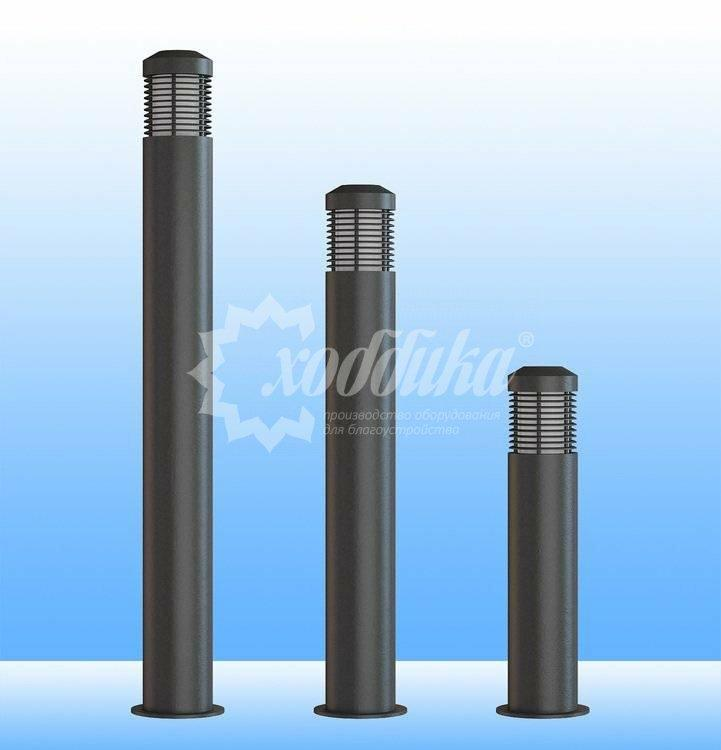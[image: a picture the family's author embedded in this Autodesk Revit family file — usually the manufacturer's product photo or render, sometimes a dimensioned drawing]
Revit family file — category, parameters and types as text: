
# Revit family: Фонарь уличный «Айрон» Арт 7549
name_source: partatom
category: Антураж
revit_build: Autodesk Revit 2018 (Build: 20180423_1000(x64)
units: mm (PartAtom-declared; Revit-internal decimal feet)

## family parameters
Всегда вертикально = Да
Источник визуального образа = Геометрия семейства
На основе рабочей плоскости = Нет
Общий = Нет
При загрузке вырезать с полостями = Нет
Точка расчета площади = Нет

## types (3) — shared parameters
URL = https://hobbyka.ru
Артикул товара = Арт. 7549
Группа модели = Светильники со стальными опорами
Длина = 159 мм
Изготовитель = ООО «Хоббика»
Изображение типоразмера = Фонарь уличный «Айрон» Арт 7549.jpg
Материал изделия = Сталь
Цвет светильника = Сталь
Ширина = 159 мм

## per-type parameters (varying)
| type | Высота | Модель 0,8 м | Модель 1,2 м | Модель 1,5 м | Описание |
| Модель 0,8 м | 800 мм | Да | Нет | Нет | Фонарь уличный «Айрон». Модель 0,8м |
| Модель 1,2 м | 1200 мм | Нет | Да | Нет | Фонарь уличный «Айрон». Модель 1,2 м |
| Модель 1,5 м | 1500 мм | Нет | Нет | Да | Фонарь уличный «Айрон». Модель 1,5 м |
